# Revit family: Matrix MAA-Mast Arm
name_source: partatom
category: Lighting Fixtures
units: mm (PartAtom-declared; Revit-internal decimal feet)

## family parameters
Cut with Voids When Loaded = No
Host = Face
Light Source = Yes
OmniClass Number = 23.80.70.14.14
OmniClass Title = Exterior Floodlights
Part Type = Normal
Room Calculation Point = No
Round Connector Dimension = Use Diameter
Shared = No

## types (7) — shared parameters
Apparent Load = 325 VA
Assembly Code = D5020280
CCT = 4k7 - 4000K, 70 CRI
Color Filter = 16777215
Default Elevation = 48 "
Description = Matrix area combines superior luminaire design with excellent versatility, performance and value in four mounting options
Dimming Lamp Color Temperature Shift = <None>
Distribution = 5R - Type 5 Rectangular
Emit Shape Visible in Rendering = No
Emit from Rectangle Length = 20 "
Emit from Rectangle Width = 26 "
Glass = White Glass
LED Engine = 325W, 37,000 lm
Lamp = LED
Load Classification = Lighting
Manufacturer = Beacon Products
Model = Matrix MAA-Mast Arm
Photometric Web File = MA-A-64L-325-4K7-5R-U.ies
Power Factor = 1
Tilt Angle = 90.00°
URL = https://www.currentlighting.com
Voltage = 120 V
Wattage Comments = 260W to 555W
Watts = 325 W

## per-type parameters (varying)
| type | Product Material |
| MAA-DB | Dark Bronze |
| MAA-BL | Black |
| MAA-WH | White |
| MAA-PS | Platinum |
| MAA-GYS | Light Grey |
| MAA-GT | Graphite |
| MAA-TT | Titanium |

## geometry (parser evidence)
native form markers: Blend x14, Sweep x5
no freeform markers — native parametric forms only
